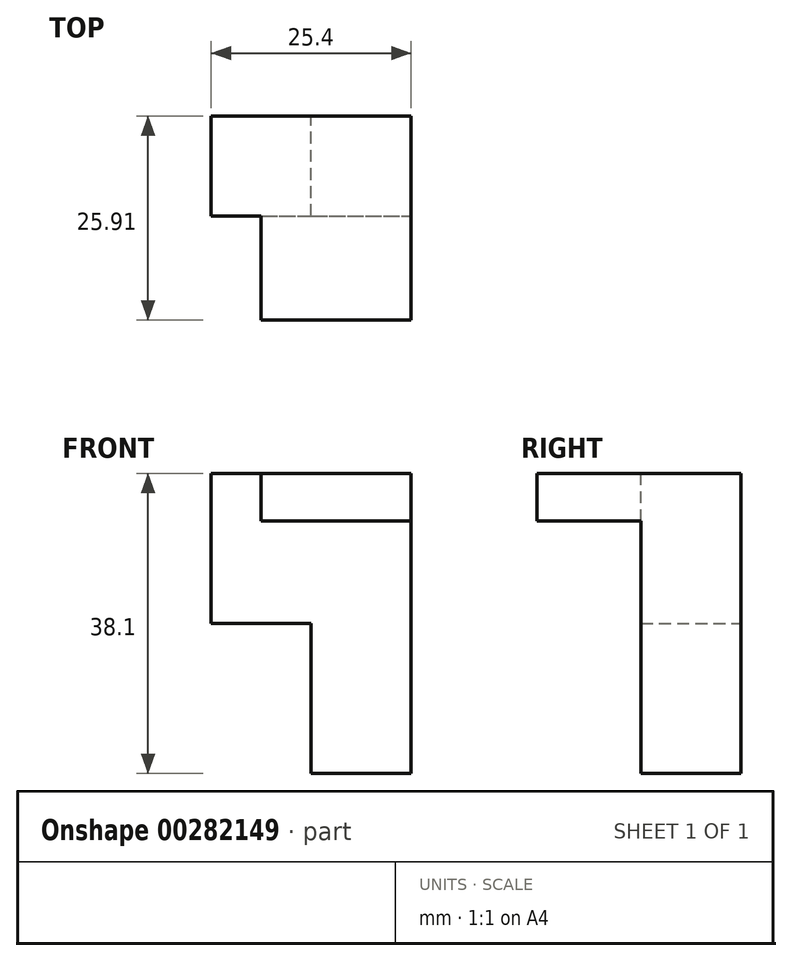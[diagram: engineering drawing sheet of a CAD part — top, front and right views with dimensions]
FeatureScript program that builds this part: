
annotation { "Feature Type Name" : "Feature", "Feature Type Description" : "" }
export const myFeature = defineFeature(function(context is Context, id is Id, definition is map)
    precondition{}
    {
        {
            var Q0;
            Q0=qCreatedBy(makeId("Front.planeOp"),FACE);
            var sketch = newSketch(context, id + "F0", { "sketchPlane" : qUnion([Q0])});
            skLineSegment(sketch, "E0", {"start": v(0, 0) * mm, "end": v(0, 38.1) * mm});
            skLineSegment(sketch, "E1", {"start": v(0, 38.1) * mm, "end": v(-25.4, 38.1) * mm});
            skLineSegment(sketch, "E2", {"start": v(-25.4, 38.1) * mm, "end": v(-25.4, 19.05) * mm});
            skLineSegment(sketch, "E3", {"start": v(-25.4, 19.05) * mm, "end": v(-12.7, 19.05) * mm});
            skLineSegment(sketch, "E4", {"start": v(-12.7, 19.05) * mm, "end": v(-12.7, 0) * mm});
            skLineSegment(sketch, "E5", {"start": v(-12.7, 0) * mm, "end": v(0, 0) * mm});
            skSolve(sketch);
        }
        {
            var Q0;
            Q0=makeQuery(id+"F0.imprint","IMPRINT",FACE,{"disambiguationData":[TD([[makeQuery(id+"F0.imprint","IMPRINT",EDGE,{"derivedFrom":sQuery(id+"F0.wireOp",EDGE,"E0")}),1.0]])]});
            extrude(context, id + "F1", {"entities" : qUnion([Q0]), "depth" : 12.7 * mm});
        }
        {
            var Q0;
            Q0=makeQuery(id+"F1.opExtrude","SWEPT_FACE",FACE,{"disambiguationData":[OSD([sQuery(id+"F0.wireOp",EDGE,"E0")])]});
            var sketch = newSketch(context, id + "F2", { "sketchPlane" : qUnion([Q0])});
            skLineSegment(sketch, "E6", {"start": v(-12.7, 38.1) * mm, "end": v(-25.91, 38.1) * mm});
            skLineSegment(sketch, "E7", {"start": v(-25.91, 38.1) * mm, "end": v(-25.91, 32.04) * mm});
            skLineSegment(sketch, "E8", {"start": v(0, 38.1) * mm, "end": v(-12.7, 38.1) * mm});
            skLineSegment(sketch, "E9", {"start": v(-25.91, 32.04) * mm, "end": v(-12.7, 32.04) * mm});
            skSolve(sketch);
        }
        {
            var Q0;
            {var subQ0=sQuery(id+"F2.wireOp",EDGE,"E6");Q0=makeQuery(id+"F2.imprint","IMPRINT",FACE,{"disambiguationData":[TD([[makeQuery(id+"F2.imprint","IMPRINT",EDGE,{"derivedFrom":subQ0}),1.0]])]});}
            extrude(context, id + "F3", {"entities" : qUnion([Q0]), "operationType" : NewBodyOperationType.ADD, "oppositeDirection" : true, "depth" : 19.05 * mm});
        }
    });
